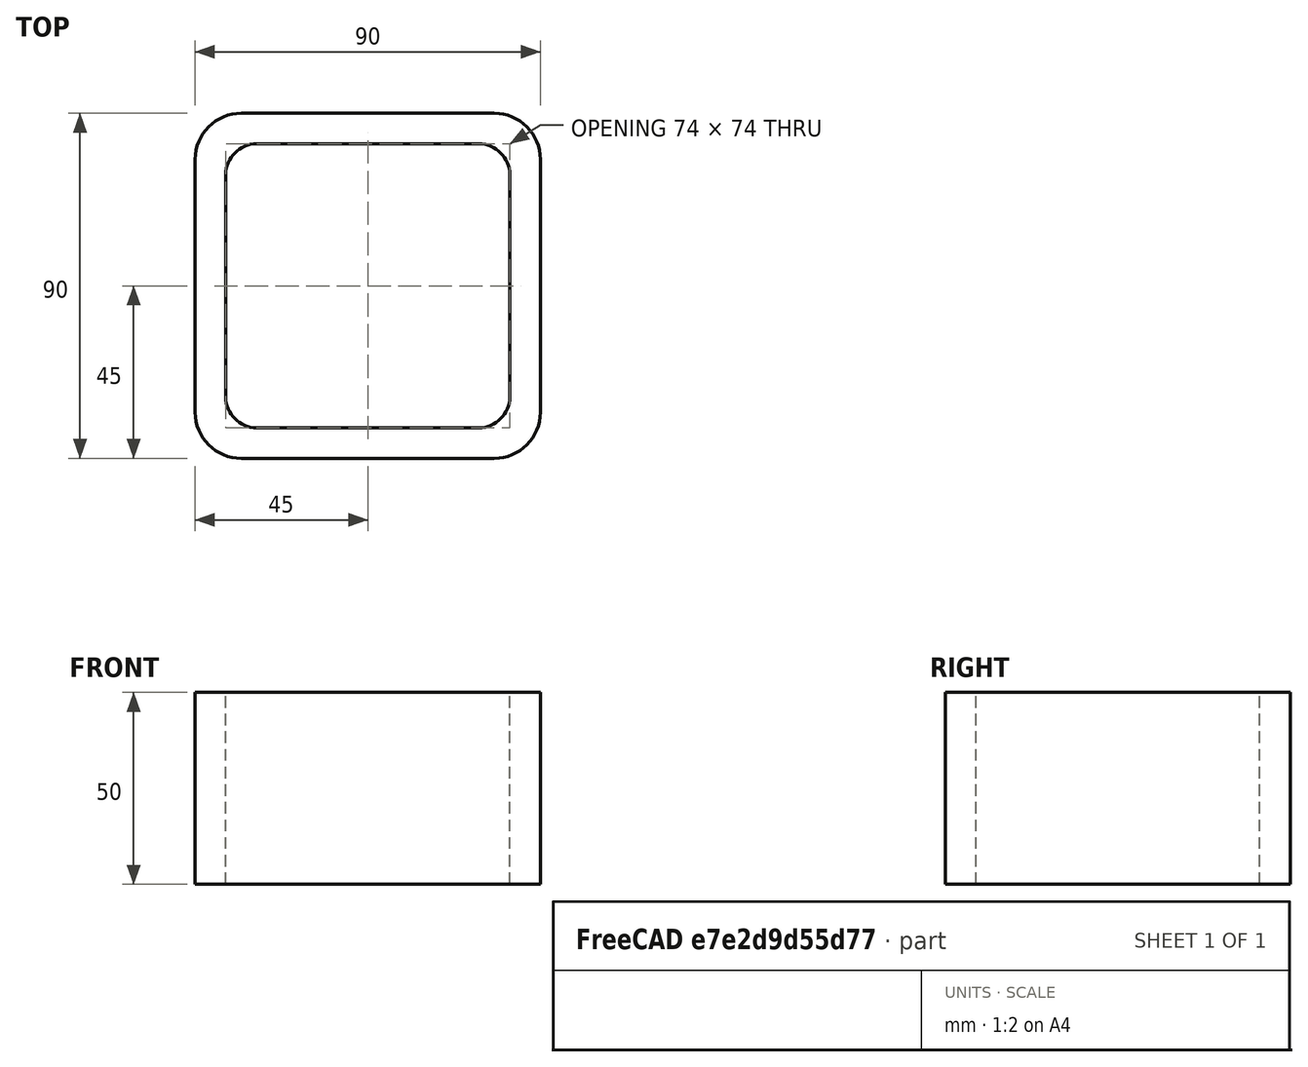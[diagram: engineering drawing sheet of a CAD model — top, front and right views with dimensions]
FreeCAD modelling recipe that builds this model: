
FCSTD DOCUMENT  (FreeCAD 0.15R4671 (Git))
Label: Square hollow section 90x90x8 EN10219 S235JRH
License: All rights reserved
LicenseURL: http://en.wikipedia.org/wiki/All_rights_reserved
objects: Sketcher::SketchObject×1, Part::Extrusion×1
note: 2 computed .brp shape members not serialized (recipe doc carries the construction recipe); baked Part::Feature solids carry a one-line shape summary decoded from their .brp

FEATURE [Sketcher::SketchObject] Sketch
  sketch-geometry (16):
    g0: LineSegment StartX=-29 StartY=37 StartZ=0 EndX=29 EndY=37 EndZ=0
    g1: LineSegment StartX=37 StartY=29 StartZ=0 EndX=37 EndY=-29 EndZ=0
    g2: LineSegment StartX=29 StartY=-37 StartZ=0 EndX=-29 EndY=-37 EndZ=0
    g3: LineSegment StartX=-37 StartY=-29 StartZ=0 EndX=-37 EndY=29 EndZ=0
    g4: LineSegment StartX=-33 StartY=45 StartZ=0 EndX=33 EndY=45 EndZ=0
    g5: LineSegment StartX=45 StartY=33 StartZ=0 EndX=45 EndY=-33 EndZ=0
    g6: LineSegment StartX=33 StartY=-45 StartZ=0 EndX=-33 EndY=-45 EndZ=0
    g7: LineSegment StartX=-45 StartY=-33 StartZ=0 EndX=-45 EndY=33 EndZ=0
    g8: ArcOfCircle CenterX=-29 CenterY=29 CenterZ=0 NormalX=0 NormalY=0 NormalZ=1 Radius=8 StartAngle=1.5708 EndAngle=3.14159
    g9: ArcOfCircle CenterX=29 CenterY=29 CenterZ=0 NormalX=0 NormalY=0 NormalZ=1 Radius=8 StartAngle=0 EndAngle=1.5708
    g10: ArcOfCircle CenterX=29 CenterY=-29 CenterZ=0 NormalX=0 NormalY=0 NormalZ=1 Radius=8 StartAngle=4.71239 EndAngle=6.28319
    g11: ArcOfCircle CenterX=-29 CenterY=-29 CenterZ=0 NormalX=0 NormalY=0 NormalZ=1 Radius=8 StartAngle=3.14159 EndAngle=4.71239
    g12: ArcOfCircle CenterX=33 CenterY=33 CenterZ=0 NormalX=0 NormalY=0 NormalZ=1 Radius=12 StartAngle=0 EndAngle=1.5708
    g13: ArcOfCircle CenterX=33 CenterY=-33 CenterZ=0 NormalX=0 NormalY=0 NormalZ=1 Radius=12 StartAngle=4.71239 EndAngle=6.28319
    g14: ArcOfCircle CenterX=-33 CenterY=-33 CenterZ=0 NormalX=0 NormalY=0 NormalZ=1 Radius=12 StartAngle=3.14159 EndAngle=4.71239
    g15: ArcOfCircle CenterX=-33 CenterY=33 CenterZ=0 NormalX=0 NormalY=0 NormalZ=1 Radius=12 StartAngle=1.5708 EndAngle=3.14159
  constraints (36):
    c: Horizontal(g2)
    c: Vertical(g3)
    c: Horizontal(g6)
    c: Vertical(g7)
    c: Tangent(g3,g8) = 1.5708
    c: Tangent(g0,g8) = 1.5708
    c: Tangent(g0,g9) = 1.5708
    c: Tangent(g1,g9) = 1.5708
    c: Tangent(g1,g10) = 1.5708
    c: Tangent(g2,g10) = 1.5708
    c: Tangent(g2,g11) = 1.5708
    c: Tangent(g3,g11) = 1.5708
    c: Tangent(g4,g12) = 1.5708
    c: Tangent(g5,g12) = 1.5708
    c: Tangent(g5,g13) = 1.5708
    c: Tangent(g6,g13) = 1.5708
    c: Tangent(g6,g14) = 1.5708
    c: Tangent(g7,g14) = 1.5708
    c: Tangent(g7,g15) = 1.5708
    c: Tangent(g4,g15) = 1.5708
    c: Equal(g9,g8)
    c: Equal(g9,g11)
    c: Equal(g9,g10)
    c: Equal(g12,g15)
    c: Equal(g12,g14)
    c: Equal(g12,g13)
    c: Symmetric(g4,g6,g-1)
    c: Symmetric(g7,g5,g-2)
    c: DistanceY(g4,g6) = -90
    c: DistanceX(g7,g5) = 90
    c: Symmetric(g3,g1,g-2)
    c: Symmetric(g0,g2,g-1)
    c: DistanceY(g0,g4) = 8
    c: DistanceX(g5,g1) = -8
    c: Radius(g9) = 8
    c: Radius(g12) = 12
FEATURE [Part::Extrusion] Extrude  label="Square hollow section 90x90x8 EN10219 S235JRH"
  Base = -> Sketch
  Dir = (0,0,50)
  Solid = true
